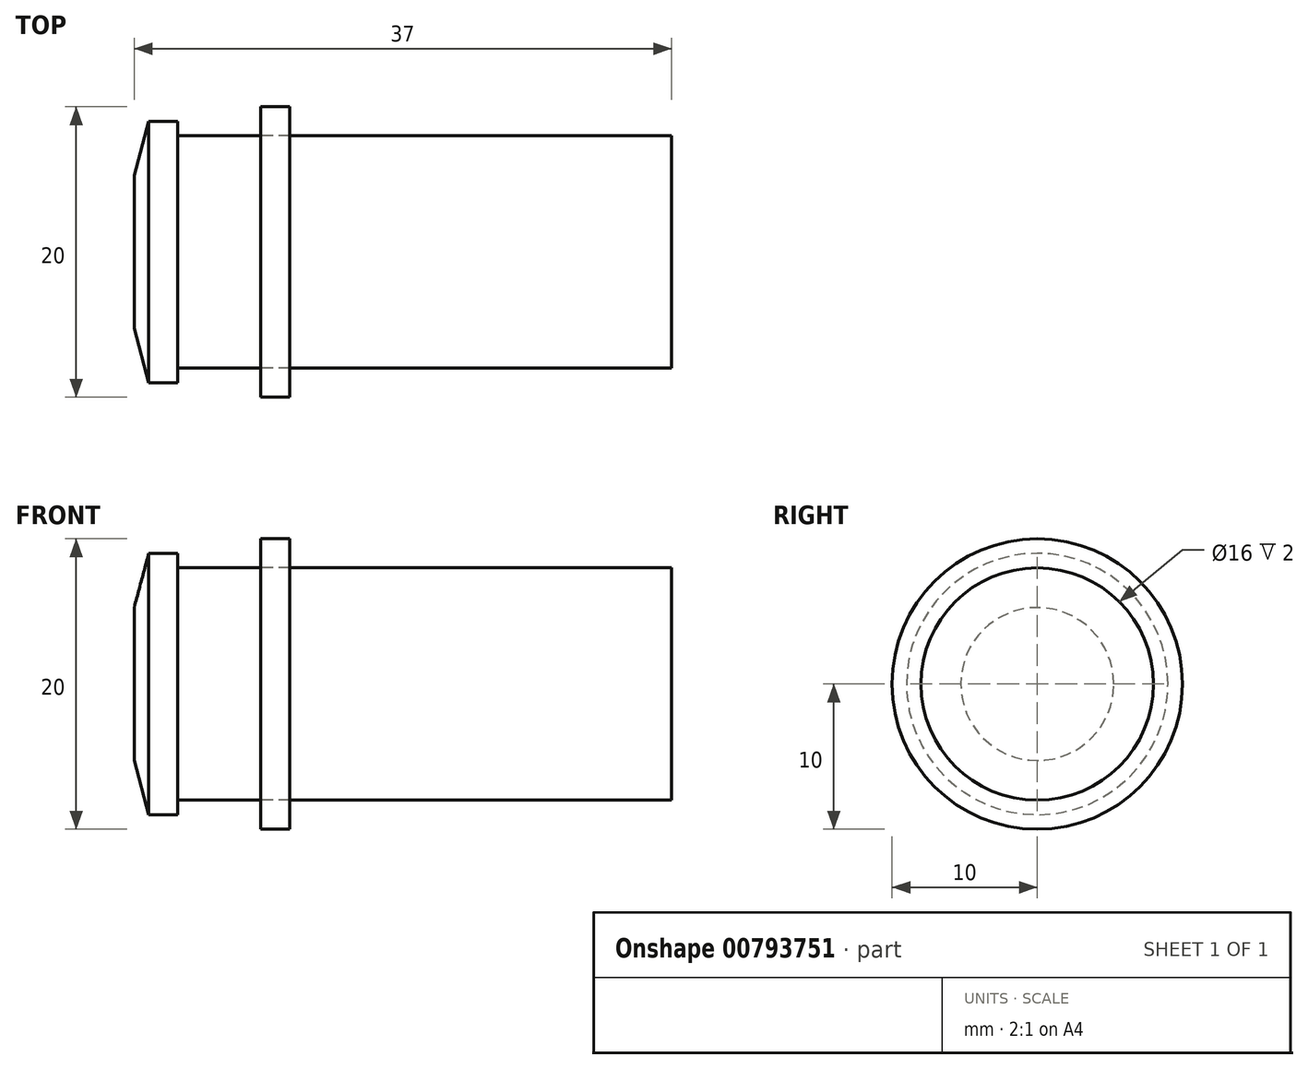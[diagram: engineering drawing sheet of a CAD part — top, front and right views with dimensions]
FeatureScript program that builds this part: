
annotation { "Feature Type Name" : "Feature", "Feature Type Description" : "" }
export const myFeature = defineFeature(function(context is Context, id is Id, definition is map)
    precondition{}
    {
        {
            var Q0;
            Q0=qCreatedBy(makeId("Top.planeOp"),FACE);
            var sketch = newSketch(context, id + "F0", { "sketchPlane" : qUnion([Q0])});
            skLineSegment(sketch, "E0", {"start": v(-37, 0) * mm, "end": v(0, 0) * mm});
            skLineSegment(sketch, "E1", {"start": v(-37, 0) * mm, "end": v(-37, 5.27) * mm});
            skLineSegment(sketch, "E2", {"start": v(-37, 5.27) * mm, "end": v(-36, 9) * mm});
            skLineSegment(sketch, "E3", {"start": v(-36, 9) * mm, "end": v(-34, 9) * mm});
            skLineSegment(sketch, "E4", {"start": v(-34, 9) * mm, "end": v(-34, 0) * mm});
            skLineSegment(sketch, "E5", {"start": v(-34, 8) * mm, "end": v(0, 8) * mm});
            skLineSegment(sketch, "E6", {"start": v(0, 8) * mm, "end": v(0, 0) * mm});
            skLineSegment(sketch, "E7", {"start": v(-28.3, 0) * mm, "end": v(-28.3, 10) * mm});
            skLineSegment(sketch, "E8", {"start": v(-28.3, 10) * mm, "end": v(-26.3, 10) * mm});
            skLineSegment(sketch, "E9", {"start": v(-26.3, 10) * mm, "end": v(-26.3, 0) * mm});
            skLineSegment(sketch, "E10.MirrorCS", {"start": v(-36, -9) * mm, "end": v(-34, -9) * mm});
            skLineSegment(sketch, "E11.MirrorCS", {"start": v(-37, 0) * mm, "end": v(-37, -5.27) * mm});
            skLineSegment(sketch, "E12.MirrorCS", {"start": v(-26.3, -10) * mm, "end": v(-26.3, 0) * mm});
            skLineSegment(sketch, "E13.MirrorCS", {"start": v(-37, -5.27) * mm, "end": v(-36, -9) * mm});
            skLineSegment(sketch, "E14.MirrorCS", {"start": v(-28.3, -10) * mm, "end": v(-26.3, -10) * mm});
            skLineSegment(sketch, "E15.MirrorCS", {"start": v(-34, -9) * mm, "end": v(-34, 0) * mm});
            skLineSegment(sketch, "E16.MirrorCS", {"start": v(-28.3, 0) * mm, "end": v(-28.3, -10) * mm});
            skLineSegment(sketch, "E17.MirrorCS", {"start": v(-34, -8) * mm, "end": v(0, -8) * mm});
            skLineSegment(sketch, "E18.MirrorCS", {"start": v(0, -8) * mm, "end": v(0, 0) * mm});
            skSolve(sketch);
        }
        {
            var Q0;
            {var subQ1=sQuery(id+"F0.wireOp",EDGE,"E1");Q0=makeQuery(id+"F0.imprint","IMPRINT",FACE,{"disambiguationData":[TD([[makeQuery(id+"F0.imprint","IMPRINT",EDGE,{"derivedFrom":subQ1}),-1.0]])]});}
            var Q1;
            {var subQ0=sQuery(id+"F0.wireOp",EDGE,"E4");var subQ5=sQuery(id+"F0.wireOp",EDGE,"E5");var subQ6=makeQuery(id+"F0.imprint","INTERSECT",VERTEX,{"derivedFrom":[subQ0,subQ5]});Q1=makeQuery(id+"F0.imprint","IMPRINT",FACE,{"disambiguationData":[TD([[makeQuery(id+"F0.imprint","IMPRINT",EDGE,{"disambiguationData":[TD([[subQ6,-1.0]])],"derivedFrom":subQ5}),-1.0]])]});}
            var Q2;
            {var subQ0=sQuery(id+"F0.wireOp",EDGE,"E7");var subQ5=sQuery(id+"F0.wireOp",EDGE,"E5");var subQ7=makeQuery(id+"F0.imprint","INTERSECT",VERTEX,{"derivedFrom":[subQ5,subQ0]});Q2=makeQuery(id+"F0.imprint","IMPRINT",FACE,{"disambiguationData":[TD([[makeQuery(id+"F0.imprint","IMPRINT",EDGE,{"disambiguationData":[TD([[subQ7,-1.0]])],"derivedFrom":subQ5}),-1.0]])]});}
            var Q3;
            {var subQ0=sQuery(id+"F0.wireOp",EDGE,"E6");Q3=makeQuery(id+"F0.imprint","IMPRINT",FACE,{"disambiguationData":[TD([[makeQuery(id+"F0.imprint","IMPRINT",EDGE,{"derivedFrom":subQ0}),-1.0]])]});}
            var Q4;
            Q4=sQuery(id+"F0.wireOp",EDGE,"E0");
            revolve(context, id + "F1", {"surfaceOperationType" : NewSurfaceOperationType.NEW, "entities" : qUnion([Q0, Q1, Q2, Q3]), "axis" : qUnion([Q4]), "revolveType" : RevolveType.FULL});
        }
        {
            var Q0;
            {var subQ5=sQuery(id+"F0.wireOp",EDGE,"E8");Q0=makeQuery(id+"F0.imprint","IMPRINT",FACE,{"disambiguationData":[TD([[makeQuery(id+"F0.imprint","IMPRINT",EDGE,{"derivedFrom":subQ5}),-1.0]])]});}
            var Q1;
            Q1=sQuery(id+"F0.wireOp",EDGE,"E0");
            revolve(context, id + "F2", {"surfaceOperationType" : NewSurfaceOperationType.NEW, "entities" : qUnion([Q0]), "axis" : qUnion([Q1]), "revolveType" : RevolveType.FULL});
        }
    });
